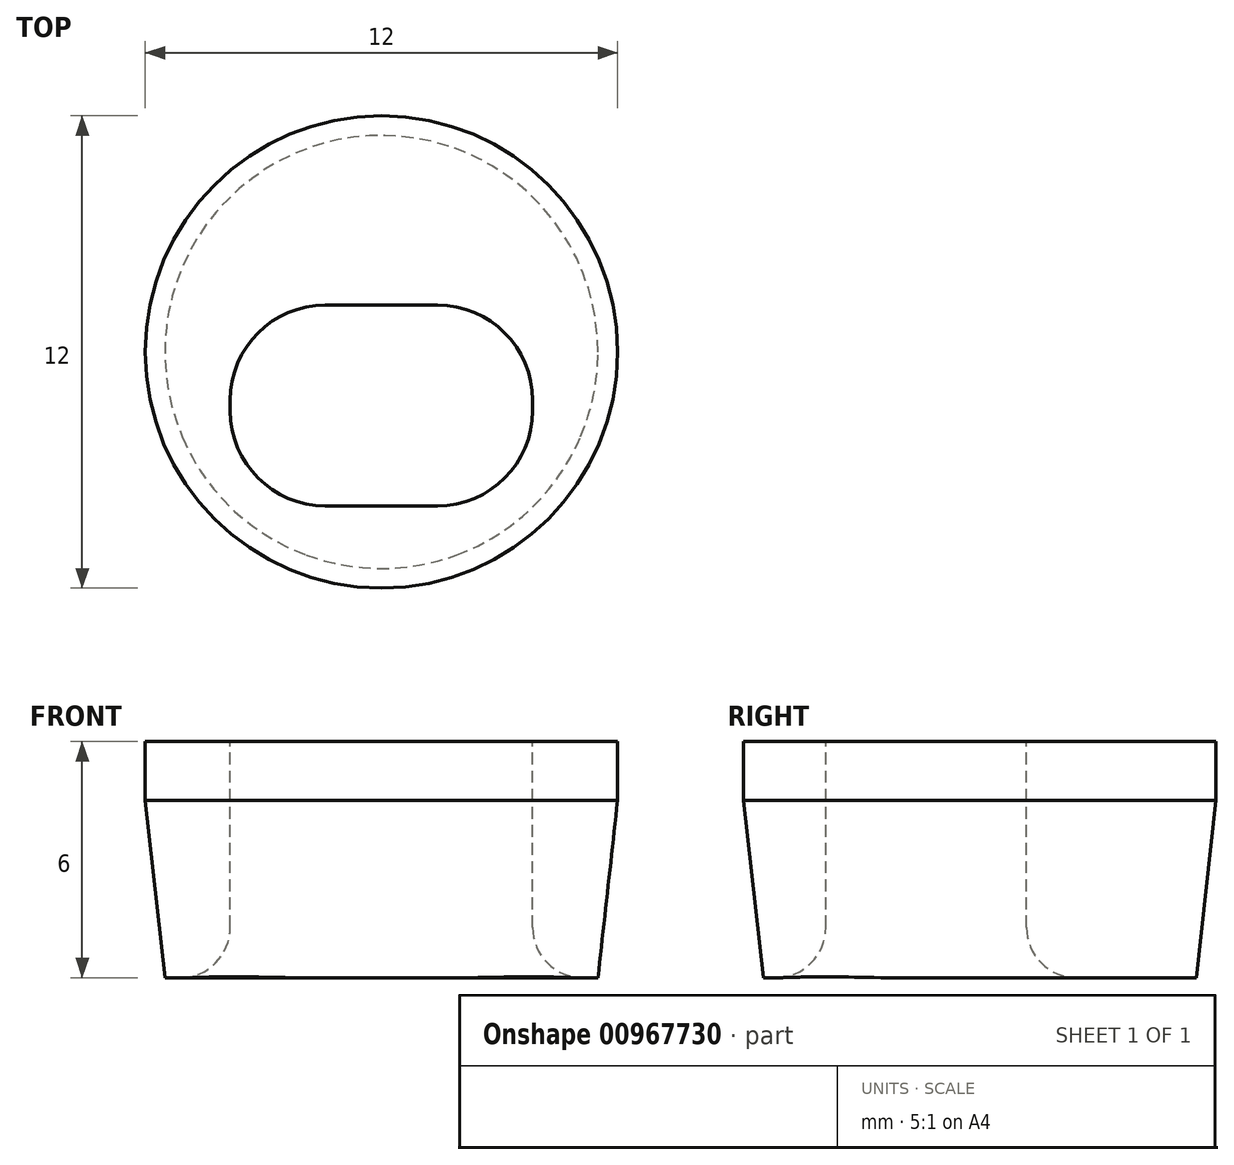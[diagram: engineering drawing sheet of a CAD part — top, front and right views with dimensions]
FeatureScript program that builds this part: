
annotation { "Feature Type Name" : "Feature", "Feature Type Description" : "" }
export const myFeature = defineFeature(function(context is Context, id is Id, definition is map)
    precondition{}
    {
        {
            var Q0;
            Q0=qCreatedBy(makeId("Top.planeOp"),FACE);
            var sketch = newSketch(context, id + "F0", { "sketchPlane" : qUnion([Q0])});
            skCircle(sketch, "E0", {"center": v(0, 0) * mm, "radius": 6 * mm});
            skSolve(sketch);
        }
        {
            var Q0;
            Q0 = qSketchRegion(id + "F0", true);
            extrude(context, id + "F1", {"entities" : qUnion([Q0]), "depth" : 6 * mm, "offsetDistance" : 25 * mm});
        }
        {
            var Q0;
            Q0=makeQuery(id+"F1.opExtrude","CAP_FACE",FACE,{"disambiguationData":[OSD([sQuery(id+"F0.wireOp",EDGE,"E0")])],"isStart":false});
            var sketch = newSketch(context, id + "F2", { "sketchPlane" : qUnion([Q0])});
            skLineSegment(sketch, "E1.bottom", {"start": v(3.84, -3.9) * mm, "end": v(-3.84, -3.9) * mm});
            skLineSegment(sketch, "E1.top", {"start": v(3.84, 1.2) * mm, "end": v(-3.84, 1.2) * mm});
            skLineSegment(sketch, "E1.left", {"start": v(3.84, -3.9) * mm, "end": v(3.84, 1.2) * mm});
            skLineSegment(sketch, "E1.right", {"start": v(-3.84, -3.9) * mm, "end": v(-3.84, 1.2) * mm});
            skPoint(sketch, "E1.middle", {"position": v(0, -1.36) * mm});
            skSolve(sketch);
        }
        {
            var Q0;
            Q0 = qSketchRegion(id + "F2", true);
            extrude(context, id + "F3", {"entities" : qUnion([Q0]), "operationType" : NewBodyOperationType.REMOVE, "oppositeDirection" : true, "depth" : 25 * mm, "offsetDistance" : 25 * mm});
        }
        {
            var Q0;
            Q0=makeQuery(id+"F3.boolean.opBoolean","COPY",EDGE,{"derivedFrom":makeQuery(id+"F3.opExtrude","SWEPT_EDGE",EDGE,{"disambiguationData":[OSD([sQuery(id+"F2.wireOp",EDGE,"E1.top"),sQuery(id+"F2.wireOp",EDGE,"E1.right")])]})});
            var Q1;
            Q1=makeQuery(id+"F3.boolean.opBoolean","COPY",EDGE,{"derivedFrom":makeQuery(id+"F3.opExtrude","SWEPT_EDGE",EDGE,{"disambiguationData":[OSD([sQuery(id+"F2.wireOp",EDGE,"E1.top"),sQuery(id+"F2.wireOp",EDGE,"E1.left")])]})});
            var Q2;
            Q2=makeQuery(id+"F3.boolean.opBoolean","COPY",EDGE,{"derivedFrom":makeQuery(id+"F3.opExtrude","SWEPT_EDGE",EDGE,{"disambiguationData":[OSD([sQuery(id+"F2.wireOp",EDGE,"E1.bottom"),sQuery(id+"F2.wireOp",EDGE,"E1.left")])]})});
            var Q3;
            Q3=makeQuery(id+"F3.boolean.opBoolean","COPY",EDGE,{"derivedFrom":makeQuery(id+"F3.opExtrude","SWEPT_EDGE",EDGE,{"disambiguationData":[OSD([sQuery(id+"F2.wireOp",EDGE,"E1.bottom"),sQuery(id+"F2.wireOp",EDGE,"E1.right")])]})});
            fillet(context, id + "F4", {"entities" : qUnion([Q0, Q1, Q2, Q3]), "radius" : 2.41 * mm, "tangentPropagation" : true, "allowEdgeOverflow" : false});
        }
        {
            var Q0;
            Q0=makeQuery(id+"F1.opExtrude","CAP_EDGE",EDGE,{"disambiguationData":[OSD([sQuery(id+"F0.wireOp",EDGE,"E0")])],"isStart":true});
            chamfer(context, id + "F5", {"entities" : qUnion([Q0]), "chamferType" : ChamferType.TWO_OFFSETS, "width1" : 4.5 * mm, "oppositeDirection" : false, "width2" : .5 * mm, "tangentPropagation" : true});
        }
        {
            var Q0;
            Q0=makeQuery(id+"F4.opFillet","BLEND_EDGE",EDGE,{"blendedFrom":[makeQuery(id+"F3.boolean.opBoolean","COPY",EDGE,{"derivedFrom":makeQuery(id+"F3.opExtrude","SWEPT_EDGE",EDGE,{"disambiguationData":[OSD([sQuery(id+"F2.wireOp",EDGE,"E1.top"),sQuery(id+"F2.wireOp",EDGE,"E1.right")])]})}),makeQuery(id+"F1.opExtrude","CAP_FACE",FACE,{"disambiguationData":[OSD([sQuery(id+"F0.wireOp",EDGE,"E0")])],"isStart":true})],"blendedInto":[makeQuery(id+"F1.opExtrude","CAP_FACE",FACE,{"disambiguationData":[OSD([sQuery(id+"F0.wireOp",EDGE,"E0")])],"isStart":true})]});
            var Q1;
            Q1=makeQuery(id+"F4.opFillet","BLEND_EDGE",EDGE,{"blendedFrom":[makeQuery(id+"F3.boolean.opBoolean","COPY",EDGE,{"derivedFrom":makeQuery(id+"F3.opExtrude","SWEPT_EDGE",EDGE,{"disambiguationData":[OSD([sQuery(id+"F2.wireOp",EDGE,"E1.bottom"),sQuery(id+"F2.wireOp",EDGE,"E1.right")])]})}),makeQuery(id+"F1.opExtrude","CAP_FACE",FACE,{"disambiguationData":[OSD([sQuery(id+"F0.wireOp",EDGE,"E0")])],"isStart":true})],"blendedInto":[makeQuery(id+"F1.opExtrude","CAP_FACE",FACE,{"disambiguationData":[OSD([sQuery(id+"F0.wireOp",EDGE,"E0")])],"isStart":true})]});
            fillet(context, id + "F6", {"entities" : qUnion([Q0, Q1]), "radius" : 1.28 * mm, "tangentPropagation" : true, "allowEdgeOverflow" : false});
        }
    });
